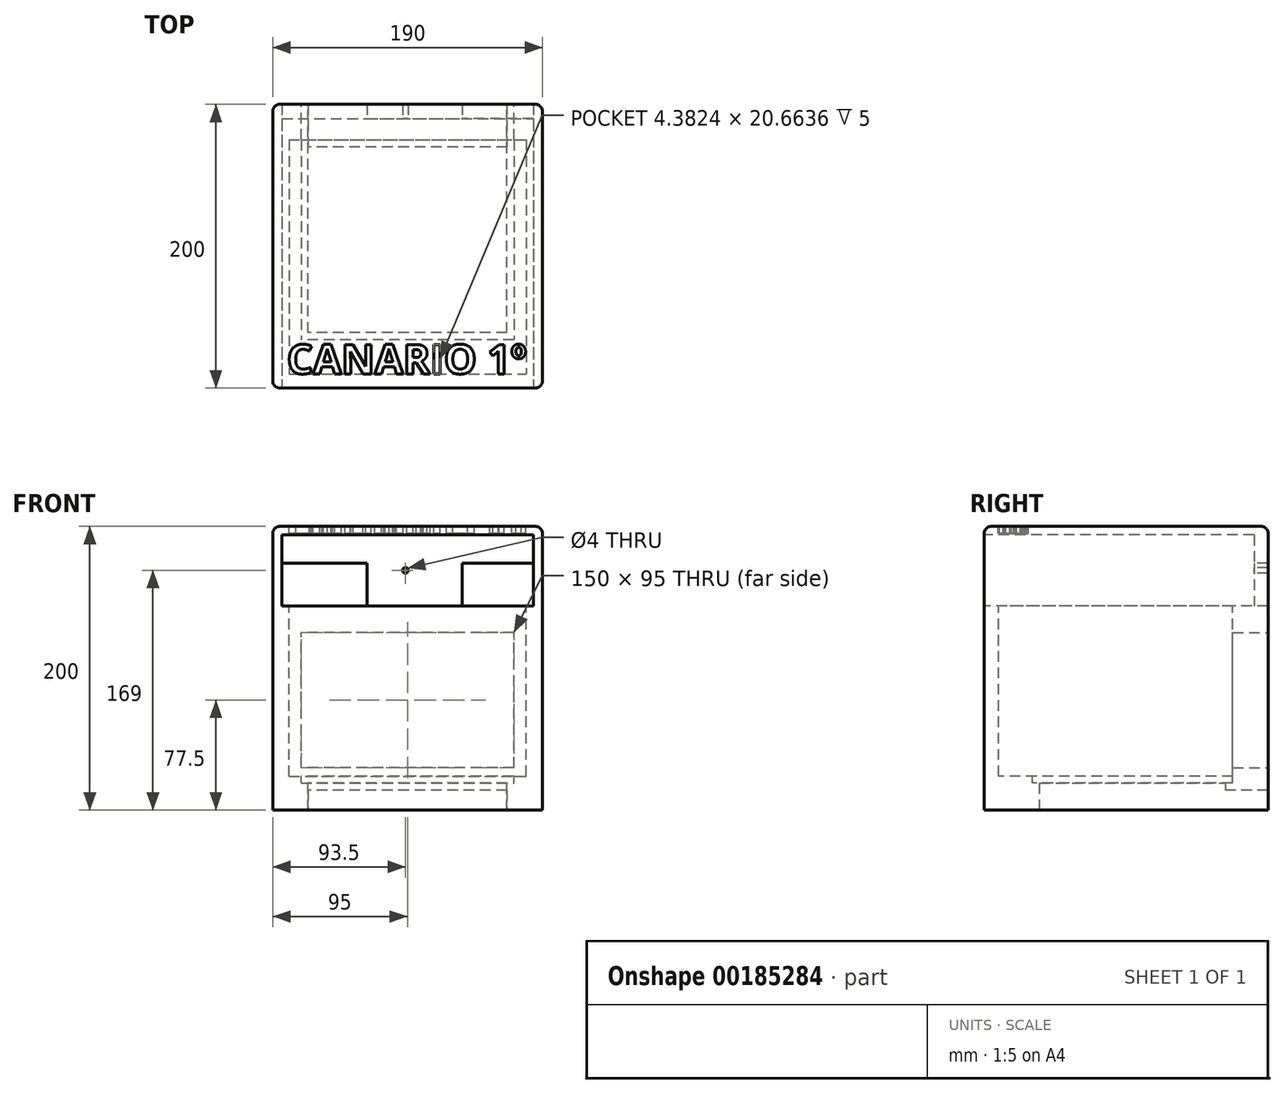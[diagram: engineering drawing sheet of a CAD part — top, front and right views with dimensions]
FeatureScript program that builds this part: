
annotation { "Feature Type Name" : "Feature", "Feature Type Description" : "" }
export const myFeature = defineFeature(function(context is Context, id is Id, definition is map)
    precondition{}
    {
        {
            var Q0;
            Q0=qCreatedBy(makeId("Top.planeOp"),FACE);
            var sketch = newSketch(context, id + "F0", { "sketchPlane" : qUnion([Q0])});
            skLineSegment(sketch, "E0.bottom", {"start": v(0, 0) * mm, "end": v(190, 0) * mm});
            skLineSegment(sketch, "E0.top", {"start": v(0, -200) * mm, "end": v(190, -200) * mm});
            skLineSegment(sketch, "E0.left", {"start": v(0, 0) * mm, "end": v(0, -200) * mm});
            skLineSegment(sketch, "E0.right", {"start": v(190, 0) * mm, "end": v(190, -200) * mm});
            skSolve(sketch);
        }
        {
            var Q0;
            Q0=makeQuery(id+"F0.imprint","IMPRINT",FACE,{"disambiguationData":[TD([[makeQuery(id+"F0.imprint","IMPRINT",EDGE,{"derivedFrom":sQuery(id+"F0.wireOp",EDGE,"E0.bottom")}),-1.0]])]});
            extrude(context, id + "F1", {"entities" : qUnion([Q0]), "depth" : 200 * mm});
        }
        {
            var Q0;
            Q0=makeQuery(id+"F1.opExtrude","SWEPT_FACE",FACE,{"disambiguationData":[OSD([sQuery(id+"F0.wireOp",EDGE,"E0.top")])]});
            var sketch = newSketch(context, id + "F2", { "sketchPlane" : qUnion([Q0])});
            skLineSegment(sketch, "E1.bottom", {"start": v(6.5, 194) * mm, "end": v(183.5, 194) * mm});
            skLineSegment(sketch, "E1.top", {"start": v(6.5, 144) * mm, "end": v(183.5, 144) * mm});
            skLineSegment(sketch, "E1.left", {"start": v(6.5, 194) * mm, "end": v(6.5, 144) * mm});
            skLineSegment(sketch, "E1.right", {"start": v(183.5, 194) * mm, "end": v(183.5, 144) * mm});
            skSolve(sketch);
        }
        {
            var Q0;
            Q0=makeQuery(id+"F2.imprint","IMPRINT",FACE,{"disambiguationData":[TD([[makeQuery(id+"F2.imprint","IMPRINT",EDGE,{"derivedFrom":sQuery(id+"F2.wireOp",EDGE,"E1.bottom")}),-1.0]])]});
            extrude(context, id + "F3", {"entities" : qUnion([Q0]), "operationType" : NewBodyOperationType.REMOVE, "oppositeDirection" : true, "depth" : 190 * mm});
        }
        {
            var Q0;
            Q0=makeQuery(id+"F3.boolean.opBoolean","COPY",FACE,{"derivedFrom":makeQuery(id+"F3.opExtrude","SWEPT_FACE",FACE,{"disambiguationData":[OSD([sQuery(id+"F2.wireOp",EDGE,"E1.top")])]})});
            var sketch = newSketch(context, id + "F4", { "sketchPlane" : qUnion([Q0])});
            skLineSegment(sketch, "E2.bottom", {"start": v(11.5, -25) * mm, "end": v(178.5, -25) * mm});
            skLineSegment(sketch, "E2.top", {"start": v(11.5, -190) * mm, "end": v(178.5, -190) * mm});
            skLineSegment(sketch, "E2.left", {"start": v(11.5, -25) * mm, "end": v(11.5, -190) * mm});
            skLineSegment(sketch, "E2.right", {"start": v(178.5, -25) * mm, "end": v(178.5, -190) * mm});
            skSolve(sketch);
        }
        {
            var Q0;
            Q0 = qSketchRegion(id + "F4", true);
            var Q1;
            Q1=makeQuery(id+"F1.opExtrude","CAP_FACE",FACE,{"disambiguationData":[OSD([sQuery(id+"F0.wireOp",EDGE,"E0.bottom"),sQuery(id+"F0.wireOp",EDGE,"E0.top"),sQuery(id+"F0.wireOp",EDGE,"E0.left"),sQuery(id+"F0.wireOp",EDGE,"E0.right")])],"isStart":true});
            var Q2;
            Q2=makeQuery(id+"F1.opExtrude","SWEPT_BODY",BODY,{"disambiguationData":[OSD([sQuery(id+"F0.wireOp",EDGE,"E0.bottom"),sQuery(id+"F0.wireOp",EDGE,"E0.top"),sQuery(id+"F0.wireOp",EDGE,"E0.left"),sQuery(id+"F0.wireOp",EDGE,"E0.right")])]});
            extrude(context, id + "F5", {"entities" : qUnion([Q0]), "operationType" : NewBodyOperationType.REMOVE, "oppositeDirection" : true, "endBoundEntityFace" : qUnion([Q1]), "endBoundEntityBody" : qUnion([Q2]), "depth" : 120 * mm});
        }
        {
            var Q0;
            Q0=makeQuery(id+"F3.boolean.opBoolean","COPY",FACE,{"derivedFrom":makeQuery(id+"F3.opExtrude","CAP_FACE",FACE,{"disambiguationData":[OSD([sQuery(id+"F2.wireOp",EDGE,"E1.bottom"),sQuery(id+"F2.wireOp",EDGE,"E1.top"),sQuery(id+"F2.wireOp",EDGE,"E1.left"),sQuery(id+"F2.wireOp",EDGE,"E1.right")])],"isStart":false})});
            var sketch = newSketch(context, id + "F6", { "sketchPlane" : qUnion([Q0])});
            skLineSegment(sketch, "E3.bottom", {"start": v(183.5, 174) * mm, "end": v(133.5, 174) * mm});
            skLineSegment(sketch, "E3.top", {"start": v(183.5, 144) * mm, "end": v(133.5, 144) * mm});
            skLineSegment(sketch, "E3.left", {"start": v(183.5, 174) * mm, "end": v(183.5, 144) * mm});
            skLineSegment(sketch, "E3.right", {"start": v(133.5, 174) * mm, "end": v(133.5, 144) * mm});
            skLineSegment(sketch, "E4.bottom", {"start": v(6.5, 174) * mm, "end": v(66.5, 174) * mm});
            skLineSegment(sketch, "E4.top", {"start": v(6.5, 144) * mm, "end": v(66.5, 144) * mm});
            skLineSegment(sketch, "E4.left", {"start": v(6.5, 174) * mm, "end": v(6.5, 144) * mm});
            skLineSegment(sketch, "E4.right", {"start": v(66.5, 174) * mm, "end": v(66.5, 144) * mm});
            skSolve(sketch);
        }
        {
            var Q0;
            Q0=makeQuery(id+"F6.imprint","IMPRINT",FACE,{"disambiguationData":[TD([[makeQuery(id+"F6.imprint","IMPRINT",EDGE,{"derivedFrom":sQuery(id+"F6.wireOp",EDGE,"E4.bottom")}),-1.0]])]});
            var Q1;
            Q1=makeQuery(id+"F6.imprint","IMPRINT",FACE,{"disambiguationData":[TD([[makeQuery(id+"F6.imprint","IMPRINT",EDGE,{"derivedFrom":sQuery(id+"F6.wireOp",EDGE,"E3.bottom")}),1.0]])]});
            extrude(context, id + "F7", {"entities" : qUnion([Q0, Q1]), "operationType" : NewBodyOperationType.REMOVE, "endBound" : BoundingType.THROUGH_ALL, "oppositeDirection" : true, "depth" : 25 * mm});
        }
        {
            var Q0;
            Q0=makeQuery(id+"F1.opExtrude","SWEPT_FACE",FACE,{"disambiguationData":[OSD([sQuery(id+"F0.wireOp",EDGE,"E0.bottom")])]});
            var sketch = newSketch(context, id + "F8", { "sketchPlane" : qUnion([Q0])});
            skLineSegment(sketch, "E5.bottom", {"start": v(-170, 30) * mm, "end": v(-20, 30) * mm});
            skLineSegment(sketch, "E5.top", {"start": v(-170, 125) * mm, "end": v(-20, 125) * mm});
            skLineSegment(sketch, "E5.left", {"start": v(-170, 30) * mm, "end": v(-170, 125) * mm});
            skLineSegment(sketch, "E5.right", {"start": v(-20, 30) * mm, "end": v(-20, 125) * mm});
            skLineSegment(sketch, "E6", {"start": v(-95, 0) * mm, "end": v(-95, 30) * mm});
            skSolve(sketch);
        }
        {
            var Q0;
            Q0=makeQuery(id+"F8.imprint","IMPRINT",FACE,{"disambiguationData":[TD([[makeQuery(id+"F8.imprint","IMPRINT",EDGE,{"derivedFrom":sQuery(id+"F8.wireOp",EDGE,"E5.top")}),-1.0]])]});
            extrude(context, id + "F9", {"entities" : qUnion([Q0]), "operationType" : NewBodyOperationType.REMOVE, "endBound" : BoundingType.UP_TO_NEXT, "oppositeDirection" : true, "depth" : 25 * mm});
        }
        {
            var Q0;
            Q0=makeQuery(id+"F5.boolean.opBoolean","COPY",FACE,{"derivedFrom":makeQuery(id+"F5.opExtrude","CAP_FACE",FACE,{"disambiguationData":[OSD([sQuery(id+"F4.wireOp",EDGE,"E2.bottom"),sQuery(id+"F4.wireOp",EDGE,"E2.top"),sQuery(id+"F4.wireOp",EDGE,"E2.left"),sQuery(id+"F4.wireOp",EDGE,"E2.right")])],"isStart":false})});
            var sketch = newSketch(context, id + "F10", { "sketchPlane" : qUnion([Q0])});
            skLineSegment(sketch, "E7.bottom", {"start": v(170, -25) * mm, "end": v(20, -25) * mm});
            skLineSegment(sketch, "E7.top", {"start": v(170, -166) * mm, "end": v(20, -166) * mm});
            skLineSegment(sketch, "E7.left", {"start": v(170, -25) * mm, "end": v(170, -166) * mm});
            skLineSegment(sketch, "E7.right", {"start": v(20, -25) * mm, "end": v(20, -166) * mm});
            skSolve(sketch);
        }
        {
            var Q0;
            Q0=makeQuery(id+"F10.imprint","IMPRINT",FACE,{"disambiguationData":[TD([[makeQuery(id+"F10.imprint","IMPRINT",EDGE,{"derivedFrom":sQuery(id+"F10.wireOp",EDGE,"E7.bottom")}),-1.0]])]});
            extrude(context, id + "F11", {"entities" : qUnion([Q0]), "operationType" : NewBodyOperationType.REMOVE, "oppositeDirection" : true, "depth" : 5 * mm});
        }
        {
            var Q0;
            Q0=makeQuery(id+"F11.boolean.opBoolean","COPY",FACE,{"derivedFrom":makeQuery(id+"F11.opExtrude","CAP_FACE",FACE,{"disambiguationData":[OSD([sQuery(id+"F10.wireOp",EDGE,"E7.bottom"),sQuery(id+"F10.wireOp",EDGE,"E7.top"),sQuery(id+"F10.wireOp",EDGE,"E7.left"),sQuery(id+"F10.wireOp",EDGE,"E7.right")])],"isStart":false})});
            var sketch = newSketch(context, id + "F12", { "sketchPlane" : qUnion([Q0])});
            skLineSegment(sketch, "E8.bottom", {"start": v(165, -161) * mm, "end": v(25, -161) * mm});
            skLineSegment(sketch, "E8.top", {"start": v(165, -30) * mm, "end": v(25, -30) * mm});
            skLineSegment(sketch, "E8.left", {"start": v(165, -161) * mm, "end": v(165, -30) * mm});
            skLineSegment(sketch, "E8.right", {"start": v(25, -161) * mm, "end": v(25, -30) * mm});
            skSolve(sketch);
        }
        {
            var Q0;
            Q0=makeQuery(id+"F12.imprint","IMPRINT",FACE,{"disambiguationData":[TD([[makeQuery(id+"F12.imprint","IMPRINT",EDGE,{"derivedFrom":sQuery(id+"F12.wireOp",EDGE,"E8.bottom")}),-1.0]])]});
            extrude(context, id + "F13", {"entities" : qUnion([Q0]), "operationType" : NewBodyOperationType.REMOVE, "endBound" : BoundingType.THROUGH_ALL, "oppositeDirection" : true, "depth" : 25 * mm});
        }
        {
            var Q0;
            Q0=makeQuery(id+"F13.boolean.opBoolean","COPY",FACE,{"derivedFrom":makeQuery(id+"F13.opExtrude","SWEPT_FACE",FACE,{"disambiguationData":[OSD([sQuery(id+"F12.wireOp",EDGE,"E8.top")])]})});
            var sketch = newSketch(context, id + "F14", { "sketchPlane" : qUnion([Q0])});
            skLineSegment(sketch, "E9.bottom", {"start": v(25, 0) * mm, "end": v(165, 0) * mm});
            skLineSegment(sketch, "E9.top", {"start": v(25, 14) * mm, "end": v(165, 14) * mm});
            skLineSegment(sketch, "E9.left", {"start": v(25, 0) * mm, "end": v(25, 14) * mm});
            skLineSegment(sketch, "E9.right", {"start": v(165, 0) * mm, "end": v(165, 14) * mm});
            skSolve(sketch);
        }
        {
            var Q0;
            Q0=makeQuery(id+"F14.imprint","IMPRINT",FACE,{"disambiguationData":[TD([[makeQuery(id+"F14.imprint","IMPRINT",EDGE,{"derivedFrom":sQuery(id+"F14.wireOp",EDGE,"E9.bottom")}),-1.0]])]});
            extrude(context, id + "F15", {"entities" : qUnion([Q0]), "operationType" : NewBodyOperationType.REMOVE, "endBound" : BoundingType.THROUGH_ALL, "oppositeDirection" : true, "depth" : 25 * mm});
        }
        {
            var Q0;
            Q0=makeQuery(id+"F3.boolean.opBoolean","COPY",FACE,{"derivedFrom":makeQuery(id+"F3.opExtrude","CAP_FACE",FACE,{"disambiguationData":[OSD([sQuery(id+"F2.wireOp",EDGE,"E1.bottom"),sQuery(id+"F2.wireOp",EDGE,"E1.top"),sQuery(id+"F2.wireOp",EDGE,"E1.left"),sQuery(id+"F2.wireOp",EDGE,"E1.right")])],"isStart":false})});
            var sketch = newSketch(context, id + "F16", { "sketchPlane" : qUnion([Q0])});
            skCircle(sketch, "E10", {"center": v(93.5, 169) * mm, "radius": 2 * mm});
            skSolve(sketch);
        }
        {
            var Q0;
            Q0=makeQuery(id+"F16.imprint","IMPRINT",FACE,{"disambiguationData":[TD([[makeQuery(id+"F16.imprint","IMPRINT",EDGE,{"derivedFrom":sQuery(id+"F16.wireOp",EDGE,"E10")}),1.0]])]});
            extrude(context, id + "F17", {"entities" : qUnion([Q0]), "operationType" : NewBodyOperationType.REMOVE, "endBound" : BoundingType.THROUGH_ALL, "oppositeDirection" : true, "depth" : 25 * mm});
        }
        {
            var Q0;
            Q0=makeQuery(id+"F1.opExtrude","CAP_FACE",FACE,{"disambiguationData":[OSD([sQuery(id+"F0.wireOp",EDGE,"E0.bottom"),sQuery(id+"F0.wireOp",EDGE,"E0.top"),sQuery(id+"F0.wireOp",EDGE,"E0.left"),sQuery(id+"F0.wireOp",EDGE,"E0.right")])],"isStart":false});
            var sketch = newSketch(context, id + "F18", { "sketchPlane" : qUnion([Q0])});
            skText(sketch, "E11", { "text": "CANARIO 1º", "fontName": "OpenSans-Bold.ttf"});
            const initialGuessF18  = {"E11": [0.01, -0.19, 1, 0, 0.02084]};
            skSetInitialGuess(sketch, initialGuessF18);
            skSolve(sketch);
        }
        {
            var Q0;
            Q0 = qSketchRegion(id + "F18", true);
            extrude(context, id + "F19", {"entities" : qUnion([Q0]), "operationType" : NewBodyOperationType.REMOVE, "oppositeDirection" : true, "depth" : 5 * mm});
        }
        {
            var Q0;
            Q0=makeQuery(id+"F1.opExtrude","CAP_EDGE",EDGE,{"disambiguationData":[OSD([sQuery(id+"F0.wireOp",EDGE,"E0.right")])],"isStart":false});
            var Q1;
            Q1=makeQuery(id+"F1.opExtrude","CAP_EDGE",EDGE,{"disambiguationData":[OSD([sQuery(id+"F0.wireOp",EDGE,"E0.top")])],"isStart":false});
            var Q2;
            Q2=makeQuery(id+"F1.opExtrude","SWEPT_EDGE",EDGE,{"disambiguationData":[OSD([sQuery(id+"F0.wireOp",EDGE,"E0.top"),sQuery(id+"F0.wireOp",EDGE,"E0.right")])]});
            var Q3;
            Q3=makeQuery(id+"F1.opExtrude","CAP_EDGE",EDGE,{"disambiguationData":[OSD([sQuery(id+"F0.wireOp",EDGE,"E0.left")])],"isStart":false});
            var Q4;
            Q4=makeQuery(id+"F1.opExtrude","SWEPT_EDGE",EDGE,{"disambiguationData":[OSD([sQuery(id+"F0.wireOp",EDGE,"E0.top"),sQuery(id+"F0.wireOp",EDGE,"E0.left")])]});
            var Q5;
            Q5=makeQuery(id+"F1.opExtrude","SWEPT_EDGE",EDGE,{"disambiguationData":[OSD([sQuery(id+"F0.wireOp",EDGE,"E0.bottom"),sQuery(id+"F0.wireOp",EDGE,"E0.left")])]});
            var Q6;
            Q6=makeQuery(id+"F1.opExtrude","CAP_EDGE",EDGE,{"disambiguationData":[OSD([sQuery(id+"F0.wireOp",EDGE,"E0.bottom")])],"isStart":false});
            var Q7;
            Q7=makeQuery(id+"F1.opExtrude","SWEPT_EDGE",EDGE,{"disambiguationData":[OSD([sQuery(id+"F0.wireOp",EDGE,"E0.bottom"),sQuery(id+"F0.wireOp",EDGE,"E0.right")])]});
            fillet(context, id + "F20", {"entities" : qUnion([Q0, Q1, Q2, Q3, Q4, Q5, Q6, Q7]), "radius" : 5 * mm, "tangentPropagation" : true, "allowEdgeOverflow" : false});
        }
    });
